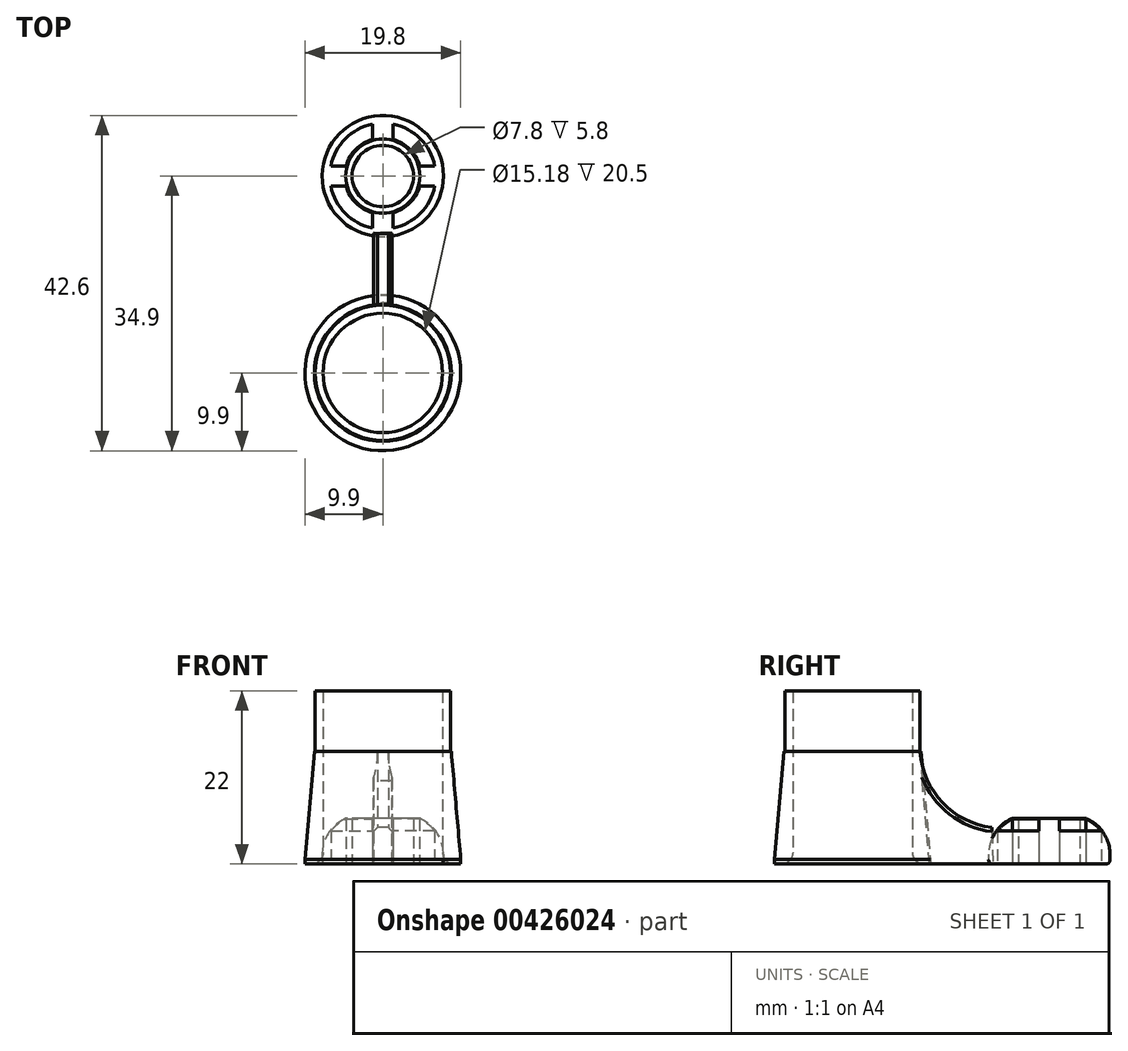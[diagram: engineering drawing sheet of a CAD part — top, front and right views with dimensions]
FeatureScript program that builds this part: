
annotation { "Feature Type Name" : "Feature", "Feature Type Description" : "" }
export const myFeature = defineFeature(function(context is Context, id is Id, definition is map)
    precondition{}
    {
        {
            var Q0;
            Q0=qCreatedBy(makeId("Top.planeOp"),FACE);
            var sketch = newSketch(context, id + "F0", { "sketchPlane" : qUnion([Q0])});
            skCircle(sketch, "E0", {"center": v(0, 0) * mm, "radius": 7.6 * mm});
            skCircle(sketch, "E1.0", {"center": v(0, 0) * mm, "radius": 8.6 * mm});
            skCircle(sketch, "E2", {"center": v(0, 0) * mm, "radius": 9.9 * mm});
            skSolve(sketch);
        }
        {
            var Q0;
            Q0=makeQuery(id+"F0.imprint","IMPRINT",FACE,{"disambiguationData":[TD([[makeQuery(id+"F0.imprint","IMPRINT",EDGE,{"derivedFrom":sQuery(id+"F0.wireOp",EDGE,"E0")}),-1.0]])]});
            extrude(context, id + "F1", {"entities" : qUnion([Q0]), "depth" : 22 * mm});
        }
        {
            var Q0;
            Q0=makeQuery(id+"F0.imprint","IMPRINT",FACE,{"disambiguationData":[TD([[makeQuery(id+"F0.imprint","IMPRINT",EDGE,{"derivedFrom":sQuery(id+"F0.wireOp",EDGE,"E1.0")}),-1.0]])]});
            extrude(context, id + "F2", {"entities" : qUnion([Q0]), "operationType" : NewBodyOperationType.ADD, "depth" : 14.3 * mm});
        }
        {
            var Q0;
            Q0=makeQuery(id+"F2.opExtrude","CAP_EDGE",EDGE,{"disambiguationData":[OSD([sQuery(id+"F0.wireOp",EDGE,"E2")])],"isStart":false});
            chamfer(context, id + "F3", {"entities" : qUnion([Q0]), "chamferType" : ChamferType.OFFSET_ANGLE, "width" : 1.2 * mm, "oppositeDirection" : false, "angle" : 85 * degree, "tangentPropagation" : true});
        }
        {
            var Q0;
            Q0=makeQuery(id+"F1.opExtrude","CAP_EDGE",EDGE,{"disambiguationData":[OSD([sQuery(id+"F0.wireOp",EDGE,"E0")])],"isStart":true});
            fillet(context, id + "F4", {"entities" : qUnion([Q0]), "radius" : 1.5 * mm, "tangentPropagation" : true, "allowEdgeOverflow" : false});
        }
        {
            var Q0;
            Q0=qCreatedBy(makeId("Top.planeOp"),FACE);
            var sketch = newSketch(context, id + "F5", { "sketchPlane" : qUnion([Q0])});
            skPoint(sketch, "E3", {"position": v(0, 25) * mm});
            skCircle(sketch, "E4", {"center": v(0, 25) * mm, "radius": 7.7 * mm});
            skCircle(sketch, "E5", {"center": v(0, 25) * mm, "radius": 4.84 * mm});
            skLineSegment(sketch, "E6", {"start": v(1.3, 32.6) * mm, "end": v(1.3, 29.67) * mm});
            skLineSegment(sketch, "E7.MirrorCS", {"start": v(-1.3, 32.6) * mm, "end": v(-1.3, 29.67) * mm});
            skLineSegment(sketch, "E8.1.0", {"start": v(-7.6, 26.3) * mm, "end": v(-4.67, 26.3) * mm});
            skLineSegment(sketch, "E8.1.1", {"start": v(-7.6, 23.7) * mm, "end": v(-4.67, 23.7) * mm});
            skLineSegment(sketch, "E8.2.0", {"start": v(-1.3, 17.4) * mm, "end": v(-1.3, 20.33) * mm});
            skLineSegment(sketch, "E8.2.1", {"start": v(1.3, 17.4) * mm, "end": v(1.3, 20.33) * mm});
            skLineSegment(sketch, "E8.3.0", {"start": v(7.6, 23.7) * mm, "end": v(4.67, 23.7) * mm});
            skLineSegment(sketch, "E8.3.1", {"start": v(7.6, 26.3) * mm, "end": v(4.67, 26.3) * mm});
            skCircle(sketch, "E9", {"center": v(0, 25) * mm, "radius": 3.9 * mm});
            skCircle(sketch, "E10", {"center": v(0, 25) * mm, "radius": 6.73 * mm});
            skSolve(sketch);
        }
        {
            var Q0;
            Q0=makeQuery(id+"F5.imprint","IMPRINT",FACE,{"disambiguationData":[TD([[makeQuery(id+"F5.imprint","IMPRINT",EDGE,{"derivedFrom":sQuery(id+"F5.wireOp",EDGE,"E9")}),-1.0]])]});
            var Q1;
            {var subQ0=sQuery(id+"F5.wireOp",EDGE,"E7.MirrorCS");var subQ1=sQuery(id+"F5.wireOp",EDGE,"E4");var subQ2=makeQuery(id+"F5.imprint","INTERSECT",VERTEX,{"derivedFrom":[subQ1,subQ0]});Q1=makeQuery(id+"F5.imprint","IMPRINT",FACE,{"disambiguationData":[TD([[makeQuery(id+"F5.imprint","IMPRINT",EDGE,{"disambiguationData":[TD([[subQ2,-1.0]])],"derivedFrom":subQ1}),1.0]])]});}
            var Q2;
            {var subQ0=sQuery(id+"F5.wireOp",EDGE,"E6");var subQ1=sQuery(id+"F5.wireOp",EDGE,"E4");var subQ2=makeQuery(id+"F5.imprint","INTERSECT",VERTEX,{"derivedFrom":[subQ1,subQ0]});Q2=makeQuery(id+"F5.imprint","IMPRINT",FACE,{"disambiguationData":[TD([[makeQuery(id+"F5.imprint","IMPRINT",EDGE,{"disambiguationData":[TD([[subQ2,-1.0]])],"derivedFrom":subQ1}),1.0]])]});}
            var Q3;
            {var subQ0=sQuery(id+"F5.wireOp",EDGE,"E6");var subQ1=sQuery(id+"F5.wireOp",EDGE,"E4");var subQ2=makeQuery(id+"F5.imprint","INTERSECT",VERTEX,{"derivedFrom":[subQ1,subQ0]});Q3=makeQuery(id+"F5.imprint","IMPRINT",FACE,{"disambiguationData":[TD([[makeQuery(id+"F5.imprint","IMPRINT",EDGE,{"disambiguationData":[TD([[subQ2,1.0]])],"derivedFrom":subQ1}),1.0]])]});}
            var Q4;
            {var subQ0=sQuery(id+"F5.wireOp",EDGE,"E8.3.0");var subQ1=sQuery(id+"F5.wireOp",EDGE,"E4");var subQ2=makeQuery(id+"F5.imprint","INTERSECT",VERTEX,{"derivedFrom":[subQ1,subQ0]});Q4=makeQuery(id+"F5.imprint","IMPRINT",FACE,{"disambiguationData":[TD([[makeQuery(id+"F5.imprint","IMPRINT",EDGE,{"disambiguationData":[TD([[subQ2,-1.0]])],"derivedFrom":subQ1}),1.0]])]});}
            var Q5;
            {var subQ0=sQuery(id+"F5.wireOp",EDGE,"E8.2.1");var subQ1=sQuery(id+"F5.wireOp",EDGE,"E4");var subQ2=makeQuery(id+"F5.imprint","INTERSECT",VERTEX,{"derivedFrom":[subQ1,subQ0]});Q5=makeQuery(id+"F5.imprint","IMPRINT",FACE,{"disambiguationData":[TD([[makeQuery(id+"F5.imprint","IMPRINT",EDGE,{"disambiguationData":[TD([[subQ2,-1.0]])],"derivedFrom":subQ1}),1.0]])]});}
            var Q6;
            {var subQ0=sQuery(id+"F5.wireOp",EDGE,"E8.2.0");var subQ1=sQuery(id+"F5.wireOp",EDGE,"E4");var subQ2=makeQuery(id+"F5.imprint","INTERSECT",VERTEX,{"derivedFrom":[subQ1,subQ0]});Q6=makeQuery(id+"F5.imprint","IMPRINT",FACE,{"disambiguationData":[TD([[makeQuery(id+"F5.imprint","IMPRINT",EDGE,{"disambiguationData":[TD([[subQ2,-1.0]])],"derivedFrom":subQ1}),1.0]])]});}
            var Q7;
            {var subQ0=sQuery(id+"F5.wireOp",EDGE,"E8.1.1");var subQ1=sQuery(id+"F5.wireOp",EDGE,"E4");var subQ2=makeQuery(id+"F5.imprint","INTERSECT",VERTEX,{"derivedFrom":[subQ1,subQ0]});Q7=makeQuery(id+"F5.imprint","IMPRINT",FACE,{"disambiguationData":[TD([[makeQuery(id+"F5.imprint","IMPRINT",EDGE,{"disambiguationData":[TD([[subQ2,-1.0]])],"derivedFrom":subQ1}),1.0]])]});}
            var Q8;
            {var subQ0=sQuery(id+"F5.wireOp",EDGE,"E8.1.0");var subQ1=sQuery(id+"F5.wireOp",EDGE,"E4");var subQ2=makeQuery(id+"F5.imprint","INTERSECT",VERTEX,{"derivedFrom":[subQ1,subQ0]});Q8=makeQuery(id+"F5.imprint","IMPRINT",FACE,{"disambiguationData":[TD([[makeQuery(id+"F5.imprint","IMPRINT",EDGE,{"disambiguationData":[TD([[subQ2,-1.0]])],"derivedFrom":subQ1}),1.0]])]});}
            var Q9;
            {var subQ0=sQuery(id+"F5.wireOp",EDGE,"E8.1.0");var subQ1=sQuery(id+"F5.wireOp",EDGE,"E5");var subQ2=makeQuery(id+"F5.imprint","INTERSECT",VERTEX,{"derivedFrom":[subQ1,subQ0]});Q9=makeQuery(id+"F5.imprint","IMPRINT",FACE,{"disambiguationData":[TD([[makeQuery(id+"F5.imprint","IMPRINT",EDGE,{"disambiguationData":[TD([[subQ2,-1.0]])],"derivedFrom":subQ1}),-1.0]])]});}
            var Q10;
            {var subQ0=sQuery(id+"F5.wireOp",EDGE,"E8.3.0");var subQ1=sQuery(id+"F5.wireOp",EDGE,"E5");var subQ2=makeQuery(id+"F5.imprint","INTERSECT",VERTEX,{"derivedFrom":[subQ1,subQ0]});Q10=makeQuery(id+"F5.imprint","IMPRINT",FACE,{"disambiguationData":[TD([[makeQuery(id+"F5.imprint","IMPRINT",EDGE,{"disambiguationData":[TD([[subQ2,-1.0]])],"derivedFrom":subQ1}),-1.0]])]});}
            var Q11;
            {var subQ0=sQuery(id+"F5.wireOp",EDGE,"E8.2.0");var subQ1=sQuery(id+"F5.wireOp",EDGE,"E5");var subQ2=makeQuery(id+"F5.imprint","INTERSECT",VERTEX,{"derivedFrom":[subQ1,subQ0]});Q11=makeQuery(id+"F5.imprint","IMPRINT",FACE,{"disambiguationData":[TD([[makeQuery(id+"F5.imprint","IMPRINT",EDGE,{"disambiguationData":[TD([[subQ2,-1.0]])],"derivedFrom":subQ1}),-1.0]])]});}
            var Q12;
            {var subQ0=sQuery(id+"F5.wireOp",EDGE,"E6");var subQ1=sQuery(id+"F5.wireOp",EDGE,"E5");var subQ2=makeQuery(id+"F5.imprint","INTERSECT",VERTEX,{"derivedFrom":[subQ1,subQ0]});Q12=makeQuery(id+"F5.imprint","IMPRINT",FACE,{"disambiguationData":[TD([[makeQuery(id+"F5.imprint","IMPRINT",EDGE,{"disambiguationData":[TD([[subQ2,-1.0]])],"derivedFrom":subQ1}),-1.0]])]});}
            extrude(context, id + "F6", {"entities" : qUnion([Q0, Q1, Q2, Q3, Q4, Q5, Q6, Q7, Q8, Q9, Q10, Q11, Q12]), "depth" : 5.8 * mm});
        }
        {
            var Q0;
            Q0=qCreatedBy(makeId("Right.planeOp"),FACE);
            var sketch = newSketch(context, id + "F7", { "sketchPlane" : qUnion([Q0])});
            skLineSegment(sketch, "E11", {"start": v(17.83, 0) * mm, "end": v(9.8, 0) * mm});
            skLineSegment(sketch, "E12", {"start": v(9.8, 0) * mm, "end": v(8.85, 10.58) * mm});
            skLineSegment(sketch, "E13", {"start": v(8.85, 10.58) * mm, "end": v(8.59, 14.26) * mm});
            skArc(sketch, "E14", {"start": v(8.59, 14.26) * mm, "mid": v(11.42, 7.82) * mm, "end": v(17.7, 4.63) * mm});
            skLineSegment(sketch, "E15", {"start": v(17.7, 4.63) * mm, "end": v(17.83, 0) * mm});
            skSolve(sketch);
        }
        {
            var Q0;
            Q0=makeQuery(id+"F7.imprint","IMPRINT",FACE,{"disambiguationData":[TD([[makeQuery(id+"F7.imprint","IMPRINT",EDGE,{"derivedFrom":sQuery(id+"F7.wireOp",EDGE,"E11")}),-1.0]])]});
            extrude(context, id + "F8", {"entities" : qUnion([Q0]), "endBound" : BoundingType.SYMMETRIC, "depth" : 2.4 * mm});
        }
        {
            var Q0;
            Q0=makeQuery(id+"F6.opExtrude","CAP_EDGE",EDGE,{"disambiguationData":[OSD([sQuery(id+"F5.wireOp",EDGE,"E4")])],"isStart":false});
            chamfer(context, id + "F9", {"entities" : qUnion([Q0]), "chamferType" : ChamferType.OFFSET_ANGLE, "width" : 3 * mm, "oppositeDirection" : false, "angle" : 20 * degree, "tangentPropagation" : true});
        }
        {
            var Q0;
            Q0=makeQuery(id+"F6.opExtrude","CAP_EDGE",EDGE,{"disambiguationData":[OSD([sQuery(id+"F5.wireOp",EDGE,"E4")])],"isStart":true});
            fillet(context, id + "F10", {"entities" : qUnion([Q0]), "radius" : .5 * mm, "tangentPropagation" : true, "allowEdgeOverflow" : false});
        }
        {
            var Q0;
            Q0=makeQuery(id+"F8.opExtrude","CAP_EDGE",EDGE,{"disambiguationData":[OSD([sQuery(id+"F7.wireOp",EDGE,"E14")])],"isStart":true});
            var Q1;
            Q1=makeQuery(id+"F8.opExtrude","CAP_EDGE",EDGE,{"disambiguationData":[OSD([sQuery(id+"F7.wireOp",EDGE,"E14")])],"isStart":false});
            chamfer(context, id + "F11", {"entities" : qUnion([Q0, Q1]), "width" : .5 * mm, "tangentPropagation" : true});
        }
        {
            var Q0;
            {var subQ0=sQuery(id+"F5.wireOp",EDGE,"E4");Q0=makeQuery(id+"F9.opChamfer","BLEND_EDGE",EDGE,{"blendedFrom":[makeQuery(id+"F6.opExtrude","CAP_EDGE",EDGE,{"disambiguationData":[OSD([subQ0])],"isStart":false}),makeQuery(id+"F6.opExtrude","SWEPT_FACE",FACE,{"disambiguationData":[OSD([subQ0])]})],"blendedInto":[makeQuery(id+"F6.opExtrude","SWEPT_FACE",FACE,{"disambiguationData":[OSD([subQ0])]})]});}
            fillet(context, id + "F12", {"entities" : qUnion([Q0]), "radius" : 5 * mm, "tangentPropagation" : true, "allowEdgeOverflow" : false});
        }
    });
